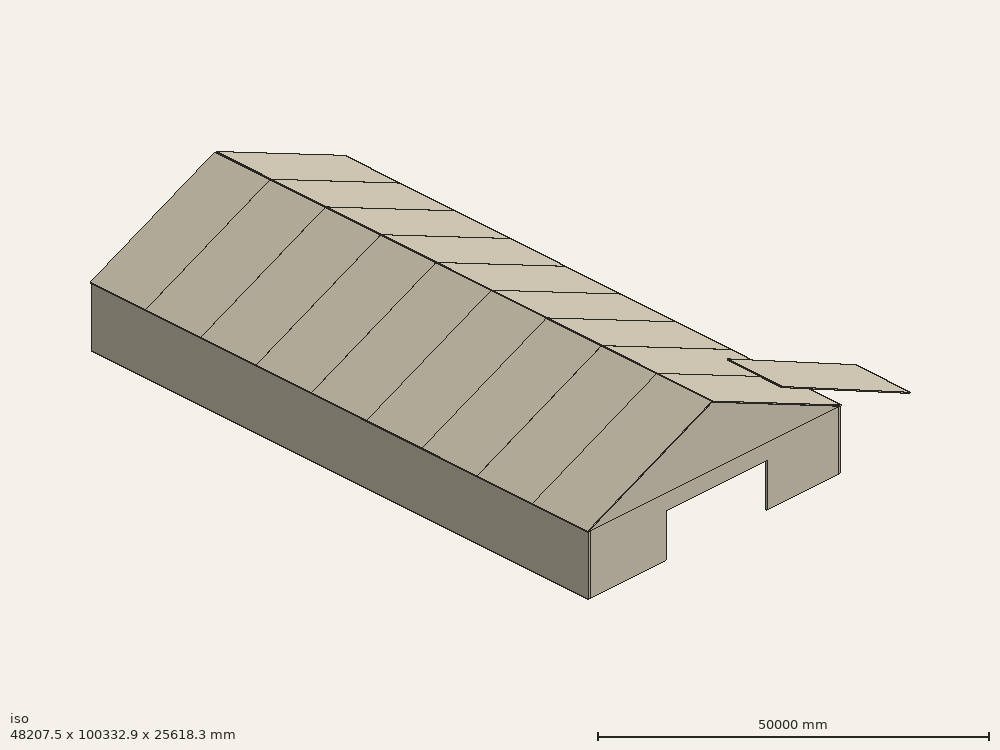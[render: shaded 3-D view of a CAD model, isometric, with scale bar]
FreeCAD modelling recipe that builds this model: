
FCSTD DOCUMENT  (FreeCAD 0.18R4 (GitTag))
Label: Fabrication Tent
License: All rights reserved
LicenseURL: http://en.wikipedia.org/wiki/All_rights_reserved
objects: Part::Box×31, Part::Cut×6, Part::MultiFuse×3, App::DocumentObjectGroup×1
note: 40 computed .brp shape members not serialized (recipe doc carries the construction recipe); baked Part::Feature solids carry a one-line shape summary decoded from their .brp

FEATURE [Part::Box] Box  label="Wall 1S"
  AttacherType = Attacher::AttachEngine3D
  Height = 9999.88
  Length = 45000.4
  Placement = pos=(228.6,-7018.02,0) rot=(0,0,1;0rad)
  Width = 304.8
FEATURE [Part::Box] Box001  label="Wall 2S"
  AttacherType = Attacher::AttachEngine3D
  Height = 9999.88
  Length = 45000.4
  Placement = pos=(228.6,82677,0) rot=(0,0,1;0rad)
  Width = 304.8
FEATURE [Part::Box] Box002  label="Wall 1L"
  AttacherType = Attacher::AttachEngine3D
  Height = 9999.88
  Length = 90000
  Placement = pos=(-76.2,82981.8,0) rot=(0,0,-1;1.5708rad)
  Width = 304.8
FEATURE [Part::Box] Box003  label="Wall 2L"
  AttacherType = Attacher::AttachEngine3D
  Height = 9999.88
  Length = 90000
  Placement = pos=(45228.8,82981.8,0) rot=(0,0,-1;1.5708rad)
  Width = 304.8
FEATURE [Part::Box] Box004  label="Gable End "
  AttacherType = Attacher::AttachEngine3D
  Height = 9999.88
  Length = 45610.3
  Placement = pos=(-76.2,-7018.02,10007.6) rot=(0,0,1;0rad)
  Width = 304.8
FEATURE [Part::Box] Box005  label="Cutter"
  AttacherType = Attacher::AttachEngine3D
  Height = 10000
  Length = 27432
  Placement = pos=(21494.5,-7094.22,20383.3) rot=(0,1,0;0.40928rad)
  Width = 457.2
FEATURE [Part::Box] Box006  label="Cutter001"
  AttacherType = Attacher::AttachEngine3D
  Height = 10000
  Length = 27432
  Placement = pos=(-1457.48,-7086.6,9401.1) rot=(0,-1,0;0.418879rad)
  Width = 457.2
FEATURE [Part::Cut] Cut
  Base = -> Box004
  Tool = -> Box006
FEATURE [Part::Cut] Cut001  label="Gable End 1"
  Base = -> Cut
  Tool = -> Box005
FEATURE [Part::Box] Box007  label="Cutter002"
  AttacherType = Attacher::AttachEngine3D
  Height = 10000
  Length = 27432
  Placement = pos=(-1457.48,-7086.6,9401.1) rot=(0,-1,0;0.418879rad)
  Width = 457.2
FEATURE [Part::Box] Box008  label="Gable End 002"
  AttacherType = Attacher::AttachEngine3D
  Height = 9999.88
  Length = 45610.3
  Placement = pos=(-76.2,-7018.02,10007.6) rot=(0,0,1;0rad)
  Width = 304.8
FEATURE [Part::Box] Box009  label="Cutter003"
  AttacherType = Attacher::AttachEngine3D
  Height = 10000
  Length = 27432
  Placement = pos=(21494.5,-7094.22,20383.3) rot=(0,1,0;0.40928rad)
  Width = 457.2
FEATURE [Part::Cut] Cut003
  Base = -> Box008
  Tool = -> Box007
FEATURE [Part::Cut] Cut002  label="Gable End 2"
  Base = -> Cut003
  Placement = pos=(0,89691.2,35.56) rot=(0,0,1;0rad)
  Tool = -> Box009
FEATURE [Part::Box] Box010  label="Roof Panel"
  AttacherType = Attacher::AttachEngine3D
  Height = 9966.96
  Length = 25374.6
  Placement = pos=(24637,-7383.93,25479) rot=(0.957737,0.203218,-0.203573;1.61571rad)
  Width = 152.4
FEATURE [Part::Box] Box011  label="Roof Panel 1"
  AttacherType = Attacher::AttachEngine3D
  Height = 10000
  Length = 24688.8
  Placement = pos=(-2329.18,2969.01,20264.6) rot=(1,0,0;1.57254rad)
  Width = 152.4
FEATURE [Part::Box] Box012  label="Roof Panel 002"
  AttacherType = Attacher::AttachEngine3D
  Height = 10000
  Length = 24688.8
  Placement = pos=(-2329.18,12970.2,20282) rot=(1,0,0;1.57254rad)
  Width = 152.4
FEATURE [Part::Box] Box013  label="Roof Panel 003"
  AttacherType = Attacher::AttachEngine3D
  Height = 10000
  Length = 24688.8
  Placement = pos=(-2329.18,22953.7,20299.4) rot=(1,0,0;1.57254rad)
  Width = 152.4
FEATURE [Part::Box] Box014  label="Roof Panel 004"
  AttacherType = Attacher::AttachEngine3D
  Height = 10000
  Length = 24688.8
  Placement = pos=(-2329.18,32954.9,20316.9) rot=(1,0,0;1.57254rad)
  Width = 152.4
FEATURE [Part::Box] Box015  label="Roof Panel 005"
  AttacherType = Attacher::AttachEngine3D
  Height = 10000
  Length = 24688.8
  Placement = pos=(-2329.18,42956.2,20334.4) rot=(1,0,0;1.57254rad)
  Width = 152.4
FEATURE [Part::Box] Box016  label="Roof Panel 006"
  AttacherType = Attacher::AttachEngine3D
  Height = 10000
  Length = 24688.8
  Placement = pos=(-2329.18,52966.3,20351.8) rot=(1,0,0;1.57254rad)
  Width = 152.4
FEATURE [Part::Box] Box017  label="Roof Panel 007"
  AttacherType = Attacher::AttachEngine3D
  Height = 10000
  Length = 24688.8
  Placement = pos=(-2329.18,62976.4,20369.3) rot=(1,0,0;1.57254rad)
  Width = 152.4
FEATURE [Part::Box] Box018  label="Roof Panel 008"
  AttacherType = Attacher::AttachEngine3D
  Height = 10000
  Length = 24688.8
  Placement = pos=(-2329.18,72968.8,20386.7) rot=(1,0,0;1.57254rad)
  Width = 152.4
FEATURE [Part::Box] Box019  label="Roof Panel 009"
  AttacherType = Attacher::AttachEngine3D
  Height = 10000
  Length = 24688.8
  Placement = pos=(-2329.18,82961.1,20404.2) rot=(1,0,0;1.57254rad)
  Width = 152.4
FEATURE [Part::MultiFuse] Fusion  label="Roof Left"
  Placement = pos=(10161.2,0,-7555.2) rot=(0,-1,0;0.418879rad)
  Shapes = -> [Box011,Box016,Box012,Box014,Box015,Box017,Box013,Box019,Box018]
FEATURE [Part::Box] Box020  label="Roof Panel 010"
  AttacherType = Attacher::AttachEngine3D
  Height = 10000
  Length = 25374.6
  Placement = pos=(-2329.18,52966.3,20351.8) rot=(1,0,0;1.57254rad)
  Width = 152.4
FEATURE [Part::Box] Box021  label="Roof Panel 011"
  AttacherType = Attacher::AttachEngine3D
  Height = 10000
  Length = 25374.6
  Placement = pos=(-2329.18,12970.2,20282) rot=(1,0,0;1.57254rad)
  Width = 152.4
FEATURE [Part::Box] Box022  label="Roof Panel 012"
  AttacherType = Attacher::AttachEngine3D
  Height = 10000
  Length = 25374.6
  Placement = pos=(-2329.18,2969.01,20264.6) rot=(1,0,0;1.57254rad)
  Width = 152.4
FEATURE [Part::Box] Box023  label="Roof Panel 013"
  AttacherType = Attacher::AttachEngine3D
  Height = 10000
  Length = 25374.6
  Placement = pos=(-2329.18,32954.9,20316.9) rot=(1,0,0;1.57254rad)
  Width = 152.4
FEATURE [Part::Box] Box024  label="Roof Panel 014"
  AttacherType = Attacher::AttachEngine3D
  Height = 10000
  Length = 25374.6
  Placement = pos=(-2329.18,42956.2,20334.4) rot=(1,0,0;1.57254rad)
  Width = 152.4
FEATURE [Part::Box] Box025  label="Roof Panel 015"
  AttacherType = Attacher::AttachEngine3D
  Height = 10000
  Length = 25374.6
  Placement = pos=(-2329.18,62976.4,20369.3) rot=(1,0,0;1.57254rad)
  Width = 152.4
FEATURE [Part::Box] Box026  label="Roof Panel 016"
  AttacherType = Attacher::AttachEngine3D
  Height = 10000
  Length = 25374.6
  Placement = pos=(-2329.18,22953.7,20299.4) rot=(1,0,0;1.57254rad)
  Width = 152.4
FEATURE [Part::Box] Box027  label="Roof Panel 017"
  AttacherType = Attacher::AttachEngine3D
  Height = 10000
  Length = 25374.6
  Placement = pos=(-2329.18,82961.1,20404.2) rot=(1,0,0;1.57254rad)
  Width = 152.4
FEATURE [Part::Box] Box028  label="Roof Panel 018"
  AttacherType = Attacher::AttachEngine3D
  Height = 10000
  Length = 25374.6
  Placement = pos=(-2329.18,72968.8,20386.7) rot=(1,0,0;1.57254rad)
  Width = 152.4
FEATURE [Part::MultiFuse] Fusion001  label="Roof Right"
  Placement = pos=(16421.4,0,530.051) rot=(0,1,0;0.408407rad)
  Shapes = -> [Box022,Box020,Box021,Box023,Box024,Box025,Box026,Box027,Box028]
FEATURE [Part::Box] Box029  label="Doorway"
  AttacherType = Attacher::AttachEngine3D
  Height = 7315.2
  Length = 18288
  Placement = pos=(13975.1,-7112,-8.89) rot=(0,0,1;0rad)
  Width = 457.2
FEATURE [Part::Box] Box030  label="Doorway001"
  AttacherType = Attacher::AttachEngine3D
  Height = 7315.2
  Length = 18288
  Placement = pos=(13975.1,82570.3,-8.89) rot=(0,0,1;0rad)
  Width = 457.2
FEATURE [Part::Cut] Cut004  label="Wall East"
  Base = -> Box001
  Tool = -> Box030
FEATURE [Part::Cut] Cut005  label="Wall West"
  Base = -> Box
  Tool = -> Box029
FEATURE [Part::MultiFuse] Fusion002  label="Whole Structure"
  Shapes = -> [Box002,Box003,Cut001,Cut002,Fusion001,Fusion,Cut004,Cut005]
FEATURE [App::DocumentObjectGroup] Group  label="Building"
  Group = -> [Fusion002]
